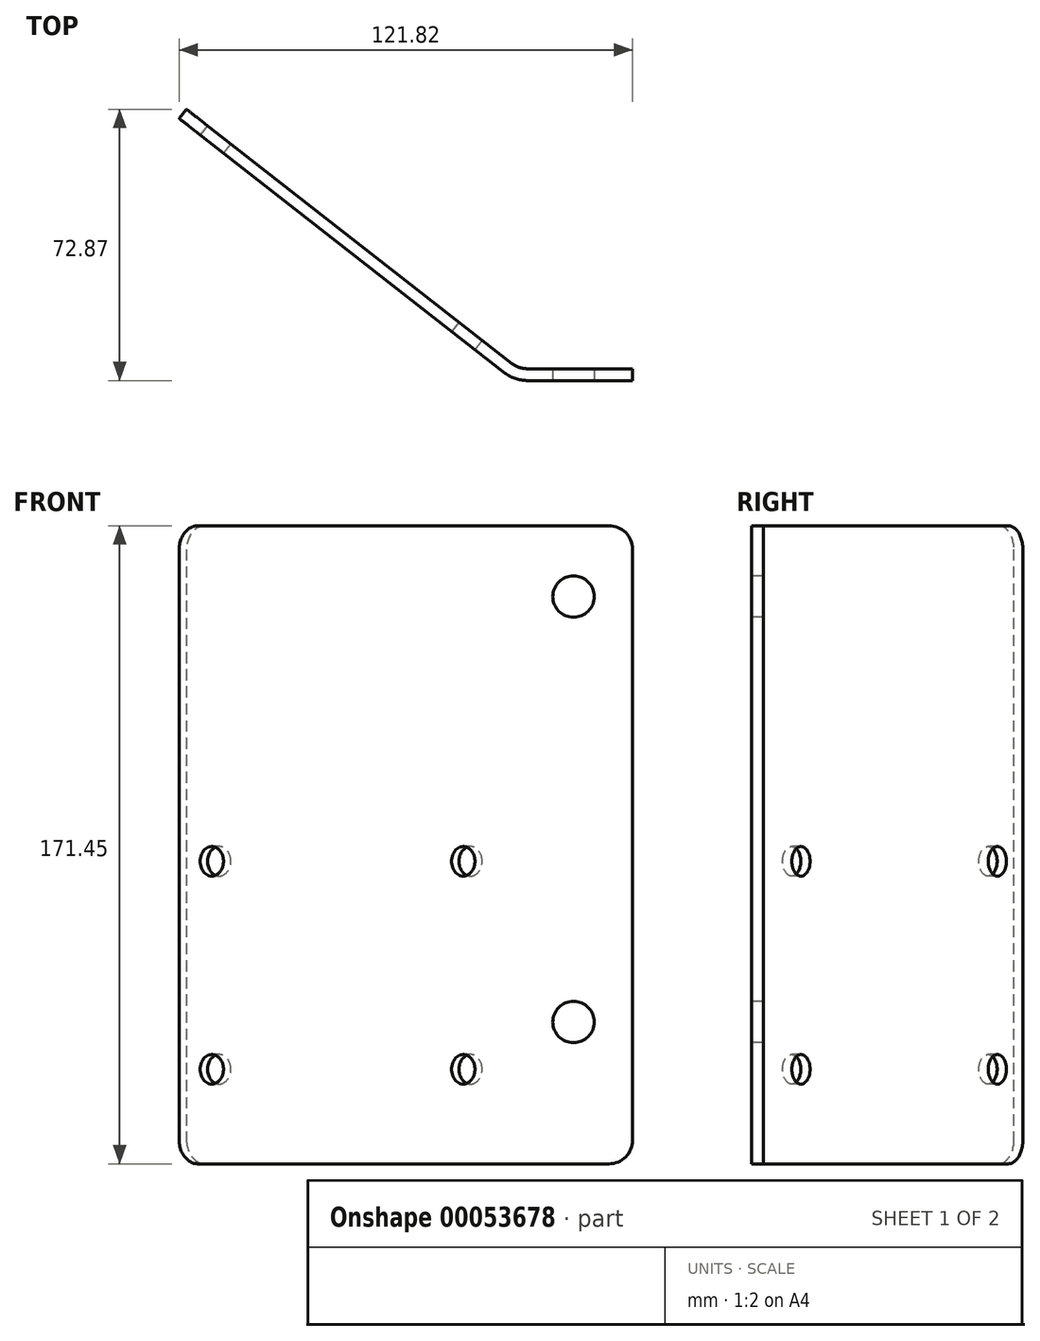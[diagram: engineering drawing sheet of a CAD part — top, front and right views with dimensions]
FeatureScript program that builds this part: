
annotation { "Feature Type Name" : "Feature", "Feature Type Description" : "" }
export const myFeature = defineFeature(function(context is Context, id is Id, definition is map)
    precondition{}
    {
        {
            var Q0;
            Q0=qCreatedBy(makeId("Top.planeOp"),FACE);
            var sketch = newSketch(context, id + "F0", { "sketchPlane" : qUnion([Q0])});
            skLineSegment(sketch, "E0", {"start": v(0, 3.17) * mm, "end": v(-28.47, 3.17) * mm});
            skLineSegment(sketch, "E1", {"start": v(-32.38, 4.52) * mm, "end": v(-119.86, 72.87) * mm});
            skLineSegment(sketch, "E2.0", {"start": v(-34.33, 2.02) * mm, "end": v(-121.82, 70.37) * mm});
            skLineSegment(sketch, "E2.2", {"start": v(0, 0) * mm, "end": v(-28.47, 0) * mm});
            skPoint(sketch, "E3", {"position": v(-31.75, 0) * mm});
            skArc(sketch, "E4", {"start": v(-32.38, 4.52) * mm, "mid": v(-30.54, 3.52) * mm, "end": v(-28.47, 3.17) * mm});
            skArc(sketch, "E2.1", {"start": v(-34.33, 2.02) * mm, "mid": v(-31.57, 0.52) * mm, "end": v(-28.47, 0) * mm});
            skLineSegment(sketch, "E5", {"start": v(0, 3.17) * mm, "end": v(0, 0) * mm});
            skLineSegment(sketch, "E6", {"start": v(-119.86, 72.87) * mm, "end": v(-121.82, 70.37) * mm});
            skSolve(sketch);
        }
        {
            var Q0;
            Q0 = qSketchRegion(id + "F0", true);
            extrude(context, id + "F1", {"entities" : qUnion([Q0]), "depth" : 171.45 * mm});
        }
        {
            var Q0;
            Q0=makeQuery(id+"F1.opExtrude","SWEPT_FACE",FACE,{"disambiguationData":[OSD([sQuery(id+"F0.wireOp",EDGE,"E2.2")])]});
            var sketch = newSketch(context, id + "F2", { "sketchPlane" : qUnion([Q0])});
            skCircle(sketch, "E7", {"center": v(-15.88, 152.4) * mm, "radius": 5.56 * mm});
            skCircle(sketch, "E8", {"center": v(-15.88, 38.1) * mm, "radius": 5.56 * mm});
            skSolve(sketch);
        }
        {
            var Q0;
            Q0 = qSketchRegion(id + "F2", true);
            extrude(context, id + "F3", {"entities" : qUnion([Q0]), "operationType" : NewBodyOperationType.REMOVE, "endBound" : BoundingType.THROUGH_ALL, "oppositeDirection" : true, "depth" : 25.4 * mm});
        }
        {
            var Q0;
            Q0=makeQuery(id+"F1.opExtrude","SWEPT_FACE",FACE,{"disambiguationData":[OSD([sQuery(id+"F0.wireOp",EDGE,"E2.0")])]});
            var sketch = newSketch(context, id + "F4", { "sketchPlane" : qUnion([Q0])});
            skCircle(sketch, "E9", {"center": v(-128.2, 81.28) * mm, "radius": 3.98 * mm});
            skCircle(sketch, "E10", {"center": v(-42.47, 81.28) * mm, "radius": 3.98 * mm});
            skCircle(sketch, "E11", {"center": v(-42.47, 25.4) * mm, "radius": 3.98 * mm});
            skCircle(sketch, "E12", {"center": v(-128.2, 25.4) * mm, "radius": 3.98 * mm});
            skSolve(sketch);
        }
        {
            var Q0;
            Q0 = qSketchRegion(id + "F4", true);
            extrude(context, id + "F5", {"entities" : qUnion([Q0]), "operationType" : NewBodyOperationType.REMOVE, "endBound" : BoundingType.THROUGH_ALL, "oppositeDirection" : true, "depth" : 25.4 * mm});
        }
        {
            var Q0;
            Q0=makeQuery(id+"F1.opExtrude","CAP_EDGE",EDGE,{"disambiguationData":[OSD([sQuery(id+"F0.wireOp",EDGE,"E6")])],"isStart":false});
            var Q1;
            Q1=makeQuery(id+"F1.opExtrude","CAP_EDGE",EDGE,{"disambiguationData":[OSD([sQuery(id+"F0.wireOp",EDGE,"E6")])],"isStart":true});
            var Q2;
            Q2=makeQuery(id+"F1.opExtrude","CAP_EDGE",EDGE,{"disambiguationData":[OSD([sQuery(id+"F0.wireOp",EDGE,"E5")])],"isStart":false});
            var Q3;
            Q3=makeQuery(id+"F1.opExtrude","CAP_EDGE",EDGE,{"disambiguationData":[OSD([sQuery(id+"F0.wireOp",EDGE,"E5")])],"isStart":true});
            fillet(context, id + "F6", {"entities" : qUnion([Q0, Q1, Q2, Q3]), "radius" : 6.35 * mm, "tangentPropagation" : true, "allowEdgeOverflow" : false});
        }
    });
